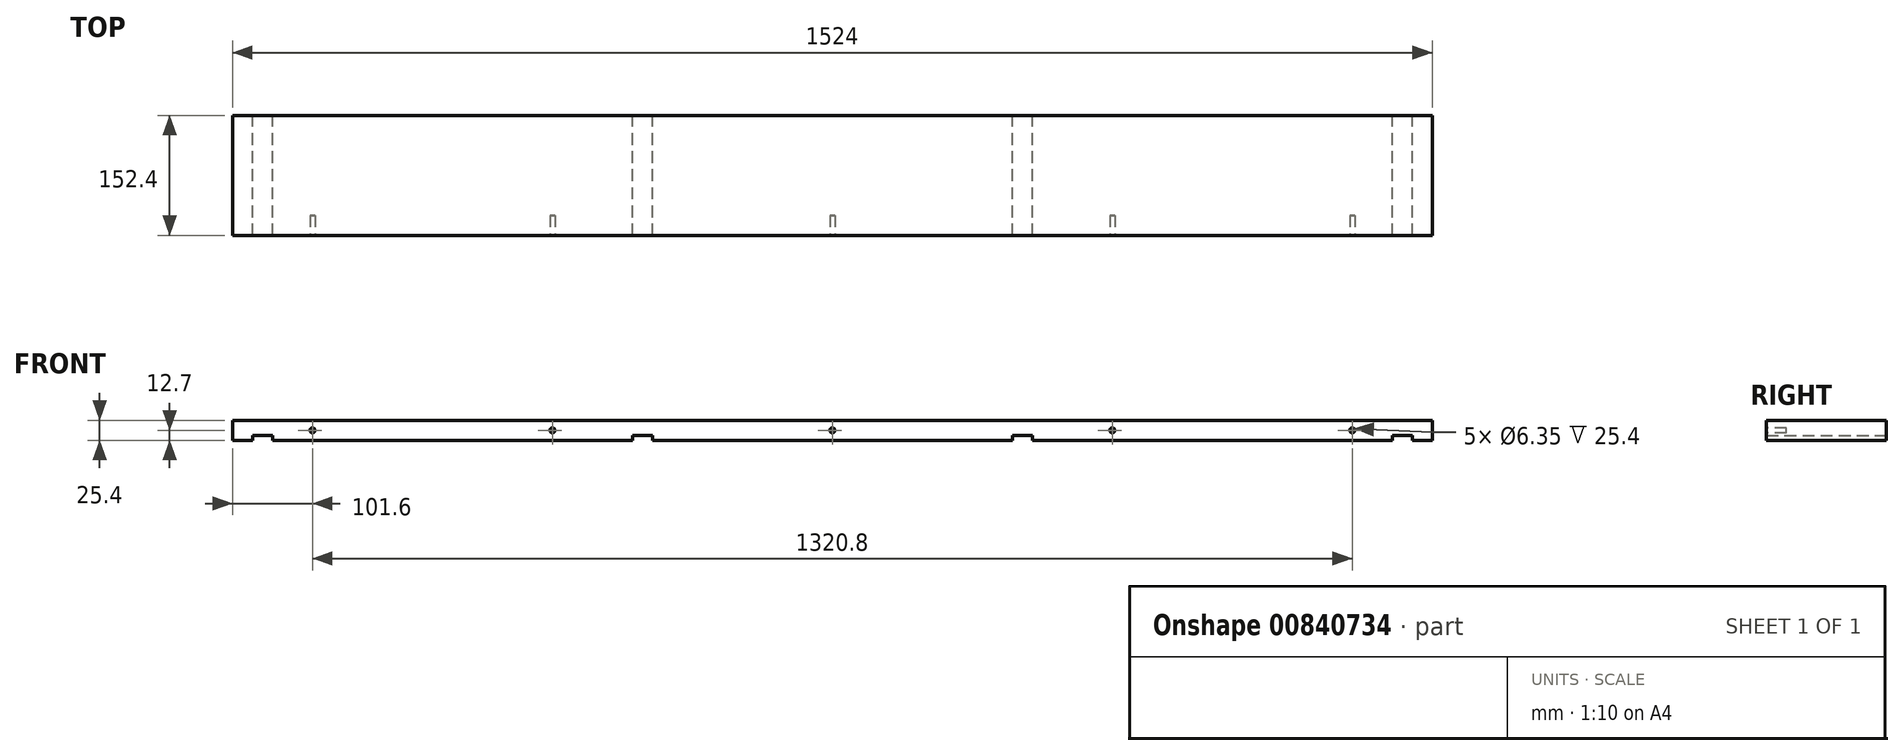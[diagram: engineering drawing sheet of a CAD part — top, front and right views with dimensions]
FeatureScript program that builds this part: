
annotation { "Feature Type Name" : "Feature", "Feature Type Description" : "" }
export const myFeature = defineFeature(function(context is Context, id is Id, definition is map)
    precondition{}
    {
        {
            var Q0;
            Q0=qCreatedBy(makeId("Top.planeOp"),FACE);
            var sketch = newSketch(context, id + "F0", { "sketchPlane" : qUnion([Q0])});
            skLineSegment(sketch, "E0.bottom", {"start": v(0, 0) * mm, "end": v(1524, 0) * mm});
            skLineSegment(sketch, "E0.top", {"start": v(0, 152.4) * mm, "end": v(1524, 152.4) * mm});
            skLineSegment(sketch, "E0.left", {"start": v(0, 0) * mm, "end": v(0, 152.4) * mm});
            skLineSegment(sketch, "E0.right", {"start": v(1524, 0) * mm, "end": v(1524, 152.4) * mm});
            skSolve(sketch);
        }
        {
            var Q0;
            Q0=makeQuery(id+"F0.imprint","IMPRINT",FACE,{"disambiguationData":[TD([[makeQuery(id+"F0.imprint","IMPRINT",EDGE,{"derivedFrom":sQuery(id+"F0.wireOp",EDGE,"E0.bottom")}),1.0]])]});
            extrude(context, id + "F1", {"entities" : qUnion([Q0]), "depth" : 25.4 * mm, "offsetDistance" : 25.4 * mm});
        }
        {
            var Q0;
            Q0=qCreatedBy(makeId("Top.planeOp"),FACE);
            var sketch = newSketch(context, id + "F2", { "sketchPlane" : qUnion([Q0])});
            skLineSegment(sketch, "E1.bottom", {"start": v(25.4, -30.93) * mm, "end": v(50.8, -30.93) * mm});
            skLineSegment(sketch, "E1.top", {"start": v(25.4, 184.97) * mm, "end": v(50.8, 184.97) * mm});
            skLineSegment(sketch, "E1.left", {"start": v(25.4, -30.93) * mm, "end": v(25.4, 184.97) * mm});
            skLineSegment(sketch, "E1.right", {"start": v(50.8, -30.93) * mm, "end": v(50.8, 184.97) * mm});
            skLineSegment(sketch, "E2.bottom", {"start": v(508, -30.93) * mm, "end": v(533.4, -30.93) * mm});
            skLineSegment(sketch, "E2.top", {"start": v(508, 184.97) * mm, "end": v(533.4, 184.97) * mm});
            skLineSegment(sketch, "E2.left", {"start": v(508, -30.93) * mm, "end": v(508, 184.97) * mm});
            skLineSegment(sketch, "E2.right", {"start": v(533.4, -30.93) * mm, "end": v(533.4, 184.97) * mm});
            skLineSegment(sketch, "E3.bottom", {"start": v(990.6, -30.93) * mm, "end": v(1016, -30.93) * mm});
            skLineSegment(sketch, "E3.top", {"start": v(990.6, 184.97) * mm, "end": v(1016, 184.97) * mm});
            skLineSegment(sketch, "E3.left", {"start": v(990.6, -30.93) * mm, "end": v(990.6, 184.97) * mm});
            skLineSegment(sketch, "E3.right", {"start": v(1016, -30.93) * mm, "end": v(1016, 184.97) * mm});
            skLineSegment(sketch, "E4.bottom", {"start": v(1473.2, -30.93) * mm, "end": v(1498.6, -30.93) * mm});
            skLineSegment(sketch, "E4.top", {"start": v(1473.2, 184.97) * mm, "end": v(1498.6, 184.97) * mm});
            skLineSegment(sketch, "E4.left", {"start": v(1473.2, -30.93) * mm, "end": v(1473.2, 184.97) * mm});
            skLineSegment(sketch, "E4.right", {"start": v(1498.6, -30.93) * mm, "end": v(1498.6, 184.97) * mm});
            skSolve(sketch);
        }
        {
            var Q0;
            Q0=makeQuery(id+"F2.imprint","IMPRINT",FACE,{"disambiguationData":[TD([[makeQuery(id+"F2.imprint","IMPRINT",EDGE,{"derivedFrom":sQuery(id+"F2.wireOp",EDGE,"E1.bottom")}),1.0]])]});
            var Q1;
            Q1=makeQuery(id+"F2.imprint","IMPRINT",FACE,{"disambiguationData":[TD([[makeQuery(id+"F2.imprint","IMPRINT",EDGE,{"derivedFrom":sQuery(id+"F2.wireOp",EDGE,"E2.bottom")}),1.0]])]});
            var Q2;
            Q2=makeQuery(id+"F2.imprint","IMPRINT",FACE,{"disambiguationData":[TD([[makeQuery(id+"F2.imprint","IMPRINT",EDGE,{"derivedFrom":sQuery(id+"F2.wireOp",EDGE,"E3.bottom")}),1.0]])]});
            var Q3;
            Q3=makeQuery(id+"F2.imprint","IMPRINT",FACE,{"disambiguationData":[TD([[makeQuery(id+"F2.imprint","IMPRINT",EDGE,{"derivedFrom":sQuery(id+"F2.wireOp",EDGE,"E4.bottom")}),1.0]])]});
            extrude(context, id + "F3", {"entities" : qUnion([Q0, Q1, Q2, Q3]), "operationType" : NewBodyOperationType.REMOVE, "depth" : 6.35 * mm, "offsetDistance" : 25.4 * mm});
        }
        {
            var Q0;
            Q0=qCreatedBy(makeId("Front.planeOp"),FACE);
            var sketch = newSketch(context, id + "F4", { "sketchPlane" : qUnion([Q0])});
            skCircle(sketch, "E5", {"center": v(101.6, 12.7) * mm, "radius": 3.18 * mm});
            skCircle(sketch, "E6", {"center": v(406.4, 12.7) * mm, "radius": 3.18 * mm});
            skCircle(sketch, "E7", {"center": v(762, 12.7) * mm, "radius": 3.18 * mm});
            skCircle(sketch, "E8", {"center": v(1117.6, 12.7) * mm, "radius": 3.18 * mm});
            skCircle(sketch, "E9", {"center": v(1422.4, 12.7) * mm, "radius": 3.18 * mm});
            skSolve(sketch);
        }
        {
            var Q0;
            Q0=makeQuery(id+"F4.imprint","IMPRINT",FACE,{"disambiguationData":[TD([[makeQuery(id+"F4.imprint","IMPRINT",EDGE,{"derivedFrom":sQuery(id+"F4.wireOp",EDGE,"E5")}),1.0]])]});
            var Q1;
            Q1=makeQuery(id+"F4.imprint","IMPRINT",FACE,{"disambiguationData":[TD([[makeQuery(id+"F4.imprint","IMPRINT",EDGE,{"derivedFrom":sQuery(id+"F4.wireOp",EDGE,"E6")}),1.0]])]});
            var Q2;
            Q2=makeQuery(id+"F4.imprint","IMPRINT",FACE,{"disambiguationData":[TD([[makeQuery(id+"F4.imprint","IMPRINT",EDGE,{"derivedFrom":sQuery(id+"F4.wireOp",EDGE,"E7")}),1.0]])]});
            var Q3;
            Q3=makeQuery(id+"F4.imprint","IMPRINT",FACE,{"disambiguationData":[TD([[makeQuery(id+"F4.imprint","IMPRINT",EDGE,{"derivedFrom":sQuery(id+"F4.wireOp",EDGE,"E8")}),1.0]])]});
            var Q4;
            Q4=makeQuery(id+"F4.imprint","IMPRINT",FACE,{"disambiguationData":[TD([[makeQuery(id+"F4.imprint","IMPRINT",EDGE,{"derivedFrom":sQuery(id+"F4.wireOp",EDGE,"E9")}),1.0]])]});
            extrude(context, id + "F5", {"entities" : qUnion([Q0, Q1, Q2, Q3, Q4]), "operationType" : NewBodyOperationType.REMOVE, "oppositeDirection" : true, "depth" : 25.4 * mm, "offsetDistance" : 25.4 * mm});
        }
    });
